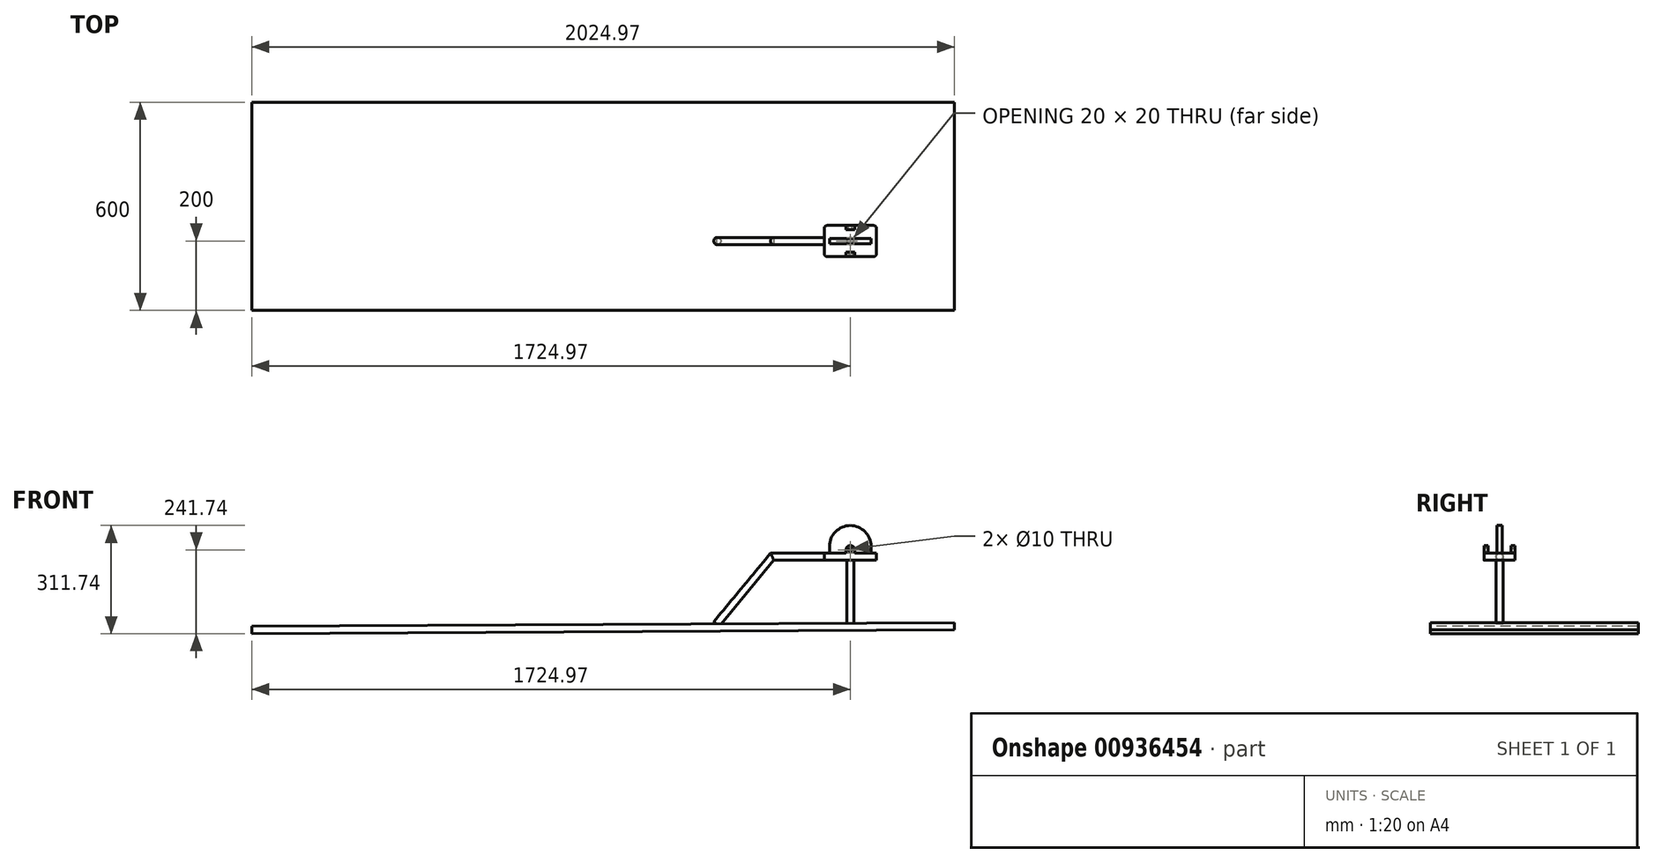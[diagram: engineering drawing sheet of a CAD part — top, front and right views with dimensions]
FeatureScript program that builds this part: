
annotation { "Feature Type Name" : "Feature", "Feature Type Description" : "" }
export const myFeature = defineFeature(function(context is Context, id is Id, definition is map)
    precondition{}
    {
        {
            var Q0;
            Q0=qCreatedBy(makeId("Right.planeOp"),FACE);
            var sketch = newSketch(context, id + "F0", { "sketchPlane" : qUnion([Q0])});
            skLineSegment(sketch, "E0", {"start": v(0, 10) * mm, "end": v(45, 10) * mm});
            skLineSegment(sketch, "E1", {"start": v(45, 10) * mm, "end": v(45, -10) * mm});
            skLineSegment(sketch, "E2", {"start": v(45, -10) * mm, "end": v(-45, -10) * mm});
            skLineSegment(sketch, "E3", {"start": v(-45, -10) * mm, "end": v(-45, 10) * mm});
            skLineSegment(sketch, "E4", {"start": v(-45, 10) * mm, "end": v(0, 10) * mm});
            skSolve(sketch);
        }
        {
            var Q0;
            Q0=makeQuery(id+"F0.imprint","IMPRINT",FACE,{"disambiguationData":[TD([[makeQuery(id+"F0.imprint","IMPRINT",EDGE,{"derivedFrom":sQuery(id+"F0.wireOp",EDGE,"E0")}),-1.0]])]});
            extrude(context, id + "F1", {"entities" : qUnion([Q0]), "depth" : 150 * mm, "offsetDistance" : 25 * mm});
        }
        {
            var Q0;
            Q0=makeQuery(id+"F1.opExtrude","SWEPT_FACE",FACE,{"disambiguationData":[OSD([sQuery(id+"F0.wireOp",EDGE,"E3")])]});
            cPlane(context, id + "F2", {"entities" : qUnion([Q0]), "cplaneType" : CPlaneType.OFFSET, "offset" : 0 * mm, "width" : 150 * mm, "height" : 150 * mm});
        }
        {
            var Q0;
            Q0=qCreatedBy(id+"F2.planeOp",FACE);
            var sketch = newSketch(context, id + "F3", { "sketchPlane" : qUnion([Q0])});
            skLineSegment(sketch, "E5", {"start": v(0, 0) * mm, "end": v(75, 0) * mm});
            skLineSegment(sketch, "E6", {"start": v(75, 0) * mm, "end": v(75, 10) * mm});
            skArc(sketch, "E7", {"start": v(87.5, 20) * mm, "mid": v(75, 32.5) * mm, "end": v(62.5, 20) * mm});
            skLineSegment(sketch, "E8", {"start": v(87.5, 20) * mm, "end": v(87.5, 10) * mm});
            skLineSegment(sketch, "E9", {"start": v(62.5, 20) * mm, "end": v(62.5, 10) * mm});
            skLineSegment(sketch, "E10", {"start": v(62.5, 10) * mm, "end": v(87.5, 10) * mm});
            skCircle(sketch, "E11", {"center": v(75, 20) * mm, "radius": 5 * mm});
            skSolve(sketch);
        }
        {
            var Q0;
            Q0=makeQuery(id+"F3.imprint","IMPRINT",FACE,{"disambiguationData":[TD([[makeQuery(id+"F3.imprint","IMPRINT",EDGE,{"derivedFrom":sQuery(id+"F3.wireOp",EDGE,"E7")}),1.0]])]});
            extrude(context, id + "F4", {"entities" : qUnion([Q0]), "operationType" : NewBodyOperationType.ADD, "oppositeDirection" : true, "depth" : 12.5 * mm, "offsetDistance" : 25 * mm});
        }
        {
            var Q0;
            Q0=makeQuery(id+"F1.opExtrude","SWEPT_FACE",FACE,{"disambiguationData":[OSD([sQuery(id+"F0.wireOp",EDGE,"E1")])]});
            cPlane(context, id + "F5", {"entities" : qUnion([Q0]), "cplaneType" : CPlaneType.OFFSET, "offset" : 0 * mm, "width" : 150 * mm, "height" : 150 * mm});
        }
        {
            var Q0;
            Q0=qCreatedBy(id+"F5.planeOp",FACE);
            var sketch = newSketch(context, id + "F6", { "sketchPlane" : qUnion([Q0])});
            skLineSegment(sketch, "E12", {"start": v(0, 0) * mm, "end": v(-75, 0) * mm});
            skLineSegment(sketch, "E13", {"start": v(-75, 0) * mm, "end": v(-75, 10) * mm});
            skArc(sketch, "E14", {"start": v(-62.5, 20) * mm, "mid": v(-75, 32.5) * mm, "end": v(-87.5, 20) * mm});
            skCircle(sketch, "E15", {"center": v(-75, 20) * mm, "radius": 5 * mm});
            skLineSegment(sketch, "E16", {"start": v(-87.5, 20) * mm, "end": v(-87.5, 10) * mm});
            skLineSegment(sketch, "E17", {"start": v(-62.5, 20) * mm, "end": v(-62.5, 10) * mm});
            skLineSegment(sketch, "E18", {"start": v(-87.5, 10) * mm, "end": v(-62.5, 10) * mm});
            skSolve(sketch);
        }
        {
            var Q0;
            Q0=makeQuery(id+"F6.imprint","IMPRINT",FACE,{"disambiguationData":[TD([[makeQuery(id+"F6.imprint","IMPRINT",EDGE,{"derivedFrom":sQuery(id+"F6.wireOp",EDGE,"E14")}),1.0]])]});
            extrude(context, id + "F7", {"entities" : qUnion([Q0]), "operationType" : NewBodyOperationType.ADD, "oppositeDirection" : true, "depth" : 12.5 * mm, "offsetDistance" : 25 * mm});
        }
        {
            var Q0;
            Q0=qCreatedBy(id+"F5.planeOp",FACE);
            cPlane(context, id + "F8", {"entities" : qUnion([Q0]), "cplaneType" : CPlaneType.OFFSET, "offset" : 45 * mm, "oppositeDirection" : true, "width" : 150 * mm, "height" : 150 * mm});
        }
        {
            var Q0;
            Q0=qCreatedBy(id+"F8.planeOp",FACE);
            var sketch = newSketch(context, id + "F9", { "sketchPlane" : qUnion([Q0])});
            skLineSegment(sketch, "E19", {"start": v(0, 0) * mm, "end": v(-75, 0) * mm});
            skLineSegment(sketch, "E20", {"start": v(-75, 0) * mm, "end": v(-75, 10) * mm});
            skLineSegment(sketch, "E21", {"start": v(-15, 30) * mm, "end": v(-15, 10) * mm});
            skLineSegment(sketch, "E22", {"start": v(-135, 30) * mm, "end": v(-135, 10) * mm});
            skLineSegment(sketch, "E23", {"start": v(-135, 10) * mm, "end": v(-15, 10) * mm});
            skArc(sketch, "E24.trimOffspring", {"start": v(-15, 30) * mm, "mid": v(-75, 90) * mm, "end": v(-135, 30) * mm});
            skSolve(sketch);
        }
        {
            var Q0;
            {var subQ2=sQuery(id+"F9.wireOp",EDGE,"E21");Q0=makeQuery(id+"F9.imprint","IMPRINT",FACE,{"disambiguationData":[TD([[makeQuery(id+"F9.imprint","IMPRINT",EDGE,{"derivedFrom":subQ2}),-1.0]])]});}
            extrude(context, id + "F10", {"entities" : qUnion([Q0]), "operationType" : NewBodyOperationType.ADD, "depth" : 7.5 * mm, "offsetDistance" : 25 * mm, "hasSecondDirection" : true, "secondDirectionOppositeDirection" : true, "secondDirectionDepth" : 7.5 * mm});
        }
        {
            var Q0;
            Q0=qCreatedBy(id+"F8.planeOp",FACE);
            var sketch = newSketch(context, id + "F11", { "sketchPlane" : qUnion([Q0])});
            skLineSegment(sketch, "E25", {"start": v(0, 0) * mm, "end": v(-75, 0) * mm});
            skLineSegment(sketch, "E26", {"start": v(-375, -190) * mm, "end": v(-375, -210) * mm});
            skLineSegment(sketch, "E27", {"start": v(0, 0) * mm, "end": v(150, 0) * mm});
            skLineSegment(sketch, "E28", {"start": v(1649.97, -200) * mm, "end": v(1649.84, -221.74) * mm});
            skLineSegment(sketch, "E29", {"start": v(-375, -210) * mm, "end": v(1649.84, -221.74) * mm});
            skLineSegment(sketch, "E30", {"start": v(1649.97, -200) * mm, "end": v(-375, -190) * mm});
            skLineSegment(sketch, "E31.trimOffspring", {"start": v(310.65, -193.39) * mm, "end": v(150, 0) * mm});
            skSolve(sketch);
        }
        {
            var Q0;
            Q0=makeQuery(id+"F1.opExtrude","CAP_FACE",FACE,{"disambiguationData":[OSD([sQuery(id+"F0.wireOp",EDGE,"E0"),sQuery(id+"F0.wireOp",EDGE,"E1"),sQuery(id+"F0.wireOp",EDGE,"E2"),sQuery(id+"F0.wireOp",EDGE,"E3"),sQuery(id+"F0.wireOp",EDGE,"E4")])],"isStart":true});
            cPlane(context, id + "F12", {"entities" : qUnion([Q0]), "cplaneType" : CPlaneType.OFFSET, "offset" : 0 * mm, "width" : 150 * mm, "height" : 150 * mm});
        }
        {
            var Q0;
            Q0=qCreatedBy(id+"F12.planeOp",FACE);
            var sketch = newSketch(context, id + "F13", { "sketchPlane" : qUnion([Q0])});
            skCircle(sketch, "E32", {"center": v(0, 0) * mm, "radius": 10 * mm});
            skSolve(sketch);
        }
        {
            var Q0;
            Q0=makeQuery(id+"F13.imprint","IMPRINT",FACE,{"disambiguationData":[TD([[makeQuery(id+"F13.imprint","IMPRINT",EDGE,{"derivedFrom":sQuery(id+"F13.wireOp",EDGE,"E32")}),1.0]])]});
            var Q1;
            Q1=sQuery(id+"F11.wireOp",EDGE,"E27");
            var Q2;
            Q2=sQuery(id+"F11.wireOp",EDGE,"E31.trimOffspring");
            sweep(context, id + "F14", {"operationType" : NewBodyOperationType.ADD, "profiles" : qUnion([Q0]), "path" : qUnion([Q1, Q2])});
        }
        {
            var Q0;
            {var subQ0=sQuery(id+"F11.wireOp",EDGE,"E26");Q0=makeQuery(id+"F11.imprint","IMPRINT",FACE,{"disambiguationData":[TD([[makeQuery(id+"F11.imprint","IMPRINT",EDGE,{"derivedFrom":subQ0}),1.0]])]});}
            extrude(context, id + "F15", {"entities" : qUnion([Q0]), "operationType" : NewBodyOperationType.ADD, "depth" : 400 * mm, "offsetDistance" : 25 * mm, "hasSecondDirection" : true, "secondDirectionOppositeDirection" : true, "secondDirectionDepth" : 200 * mm});
        }
        {
            var Q0;
            Q0=makeQuery(id+"F1.opExtrude","SWEPT_FACE",FACE,{"disambiguationData":[OSD([sQuery(id+"F0.wireOp",EDGE,"E2")])]});
            cPlane(context, id + "F16", {"entities" : qUnion([Q0]), "cplaneType" : CPlaneType.OFFSET, "offset" : 0 * mm, "width" : 150 * mm, "height" : 150 * mm});
        }
        {
            var Q0;
            Q0=qCreatedBy(id+"F16.planeOp",FACE);
            var sketch = newSketch(context, id + "F17", { "sketchPlane" : qUnion([Q0])});
            skLineSegment(sketch, "E33", {"start": v(0, 0) * mm, "end": v(75, 0) * mm});
            skCircle(sketch, "E34", {"center": v(75, 0) * mm, "radius": 10 * mm});
            skSolve(sketch);
        }
        {
            var Q0;
            Q0=makeQuery(id+"F17.imprint","IMPRINT",FACE,{"disambiguationData":[TD([[makeQuery(id+"F17.imprint","IMPRINT",EDGE,{"derivedFrom":sQuery(id+"F17.wireOp",EDGE,"E34")}),1.0]])]});
            extrude(context, id + "F18", {"entities" : qUnion([Q0]), "operationType" : NewBodyOperationType.ADD, "depth" : 190 * mm, "offsetDistance" : 25 * mm});
        }
        {
            var Q0;
            Q0=makeQuery(id+"F1.opExtrude","CAP_EDGE",EDGE,{"disambiguationData":[OSD([sQuery(id+"F0.wireOp",EDGE,"E3")])],"isStart":true});
            var Q1;
            Q1=makeQuery(id+"F1.opExtrude","CAP_EDGE",EDGE,{"disambiguationData":[OSD([sQuery(id+"F0.wireOp",EDGE,"E3")])],"isStart":false});
            var Q2;
            Q2=makeQuery(id+"F1.opExtrude","CAP_EDGE",EDGE,{"disambiguationData":[OSD([sQuery(id+"F0.wireOp",EDGE,"E1")])],"isStart":false});
            var Q3;
            Q3=makeQuery(id+"F1.opExtrude","CAP_EDGE",EDGE,{"disambiguationData":[OSD([sQuery(id+"F0.wireOp",EDGE,"E1")])],"isStart":true});
            fillet(context, id + "F19", {"entities" : qUnion([Q0, Q1, Q2, Q3]), "radius" : 8 * mm, "tangentPropagation" : true, "allowEdgeOverflow" : false});
        }
    });
